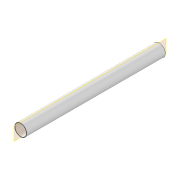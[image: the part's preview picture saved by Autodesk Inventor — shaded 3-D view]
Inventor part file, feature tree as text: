
AUTODESK INVENTOR PART (.ipt)
format: ipt  version: 2020 (Build 240168000, 168)  size: 81,920 bytes
history: native  units: mm
features: extrude x1, sketch x1
ambient origin geometry x8: Origin, YZ Plane, XZ Plane, XY Plane, X Axis, Y Axis, Z Axis, Center Point
bodies: Solid1 (feature_tree)
feature tree (2):
  extrude  "Extrusion1"  Depth=510.0mm
  sketch  "Sketch1"  dims[d0=45.0mm d1=2.0mm d2=41.0mm d3=510.0mm d4=0.0mm]
